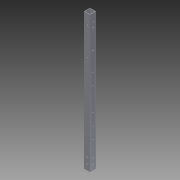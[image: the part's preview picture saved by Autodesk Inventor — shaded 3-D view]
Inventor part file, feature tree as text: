
AUTODESK INVENTOR PART (.ipt)
format: ipt  version: 2014 SP1 (Build 180222100, 222)  size: 130,048 bytes
history: native  units: in
note: dims shown in document units (in); Inventor stores cm internally (conversion verified against a paired STEP export)
features: reference x14, extrude x3, sketch x3
ambient origin geometry x8: Origin, YZ Plane, XZ Plane, XY Plane, X Axis, Y Axis, Z Axis, Center Point
bodies: Solid1 (feature_tree)
feature tree (20):
  extrude  "Extrusion1"  Depth=1.0in
  sketch  "Sketch5"  dims[d3=0.0625in d4=23.375in d5=0.0in]
  sketch  "Sketch6"  dims[d14=1.0in d15=0.0in d16=1.0in d17=0.0in]
  extrude  "Extrusion2"  Depth=23.375in TaperAngle=0.0deg
  extrude  "Extrusion3"  Depth=1.0in TaperAngle=0.0deg
  sketch  "Sketch1"  dims[d0=1.0in d2=1.0in]
  reference  "Reference10"
  reference  "Reference11"
  reference  "Reference12"
  reference  "Reference13"
  reference  "Reference14"
  reference  "Reference17"
  reference  "Reference18"
  reference  "Reference21"
  reference  "Reference22"
  reference  "Reference23"
  reference  "Reference24"
  reference  "Reference25"
  reference  "Reference26"
  reference  "Reference27"
